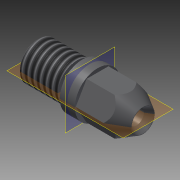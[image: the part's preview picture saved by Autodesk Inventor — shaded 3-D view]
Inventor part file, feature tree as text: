
AUTODESK INVENTOR PART (.ipt)
format: ipt  version: 2015 (Build 190159000, 159)  size: 171,520 bytes
history: native  units: mm
features: extrude x5, revolve x2, hole x2, thread x1, chamfer x1, plane x1
ambient origin geometry x8: Origin, YZ Plane, XZ Plane, XY Plane, X Axis, Y Axis, Z Axis, Center Point
bodies: Solid1 (feature_tree)
feature tree (12):
  revolve  "Revolución2"  [1 undecoded]
  thread  "Rosca2"  [1 undecoded]
  chamfer  "Chaflán1"  Angle=30.0deg  [1 undecoded]
  plane  "Plano de trabajo1"
  extrude  "Extrusión4"  TaperAngle=90.0deg  [1 undecoded]
  extrude  "Extrusión5"  Depth=19.0mm
  extrude  "Extrusión3"  Depth=19.0mm
  revolve  "Revolución1"  [1 undecoded]
  extrude  "Extrusión1"  Depth=7.0mm
  extrude  "Extrusión2"  Depth=10.0mm TaperAngle=0.0deg
  hole  "Agujero1"  [1 undecoded]
  hole  "Agujero2"  [1 undecoded]
note: 7 required parameter values undecoded (feature->parameter linkage not recoverable at this tier; creation-order binding heuristic only, values carry confidence <= 0.55)